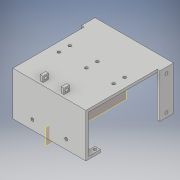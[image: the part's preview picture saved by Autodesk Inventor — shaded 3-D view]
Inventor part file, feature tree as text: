
AUTODESK INVENTOR PART (.ipt)
format: ipt  version: 2018 (Build 220112000, 112)  size: 326,656 bytes
history: native  units: mm
features: extrude x10, sketch x10, other x7, projected_geometry x3, plane x2, mirror x1
ambient origin geometry x8: Origin, YZ Plane, XZ Plane, XY Plane, X Axis, Y Axis, Z Axis, Center Point
bodies: Solid1 (feature_tree)
feature tree (33):
  other  "Wheel Base.ipt"
  extrude  "Extrusion1"  Depth=6.0mm
  extrude  "Extrusion2"  Depth=3.0mm
  extrude  "Extrusion3"  Depth=3.0mm
  extrude  "Extrusion4"  Depth=90.0mm
  extrude  "Extrusion5"  Depth=80.0mm
  extrude  "Extrusion6"  Depth=10.0mm
  extrude  "Extrusion7"  Depth=6.0mm
  extrude  "Extrusion8"  Depth=20.0mm
  extrude  "Extrusion9"  Depth=6.0mm TaperAngle=0.0deg
  extrude  "Extrusion10"  Depth=6.0mm TaperAngle=0.0deg
  mirror  "Mirror1"
  other  "TaggingFeature1"
  plane  "Work Plane1"
  sketch  "Sketch3"  dims[d0=10.0mm d2=6.0mm]
  sketch  "Sketch4"  dims[d4=3.0mm d5=0.0mm d6=3.0mm]
  sketch  "Sketch5"  dims[d7=45.0mm d8=0.0mm d9=3.0mm]
  sketch  "Sketch6"  dims[d10=90.0mm d11=0.0mm d12=3.2mm]
  projected_geometry  "Projected Loop1"
  sketch  "Sketch7"  dims[d13=37.0mm d14=80.0mm]
  sketch  "Sketch8"  dims[d15=21.5mm d16=10.0mm]
  projected_geometry  "Projected Loop2"
  other  "TaggingFeature2"
  plane  "Work Plane1_1"
  sketch  "Sketch9"  dims[d17=80.0mm d18=0.0mm d19=6.0mm]
  sketch  "Sketch11"  dims[d20=3.0mm d21=20.0mm]
  projected_geometry  "Projected Loop3"
  sketch  "Sketch12"  dims[d22=3.0mm d23=6.0mm d24=0.0mm]
  sketch  "Sketch13"  dims[d25=3.2mm d26=6.0mm d27=0.0mm d28=10.0mm d29=10.0mm d30=3.2mm d32=12.0mm d33=30.0mm d34=30.0mm d35=10.0mm d36=80.0mm d37=93.0mm d38=40.5mm d39=6.0mm d40=0.0mm d43=15.0mm d44=3.2mm d45=37.0mm d46=48.0mm d47=6.0mm d48=3.0mm d49=0.0mm d50=6.0mm d51=3.0mm d52=6.0mm d53=0.0mm d54=6.0mm d55=0.0mm]
  other  "Solid1::Wheel Base.ipt"
  other  "Srf1"
  other  "Solid1::Wheel Base.ipt_1"
  other  "Srf2"
